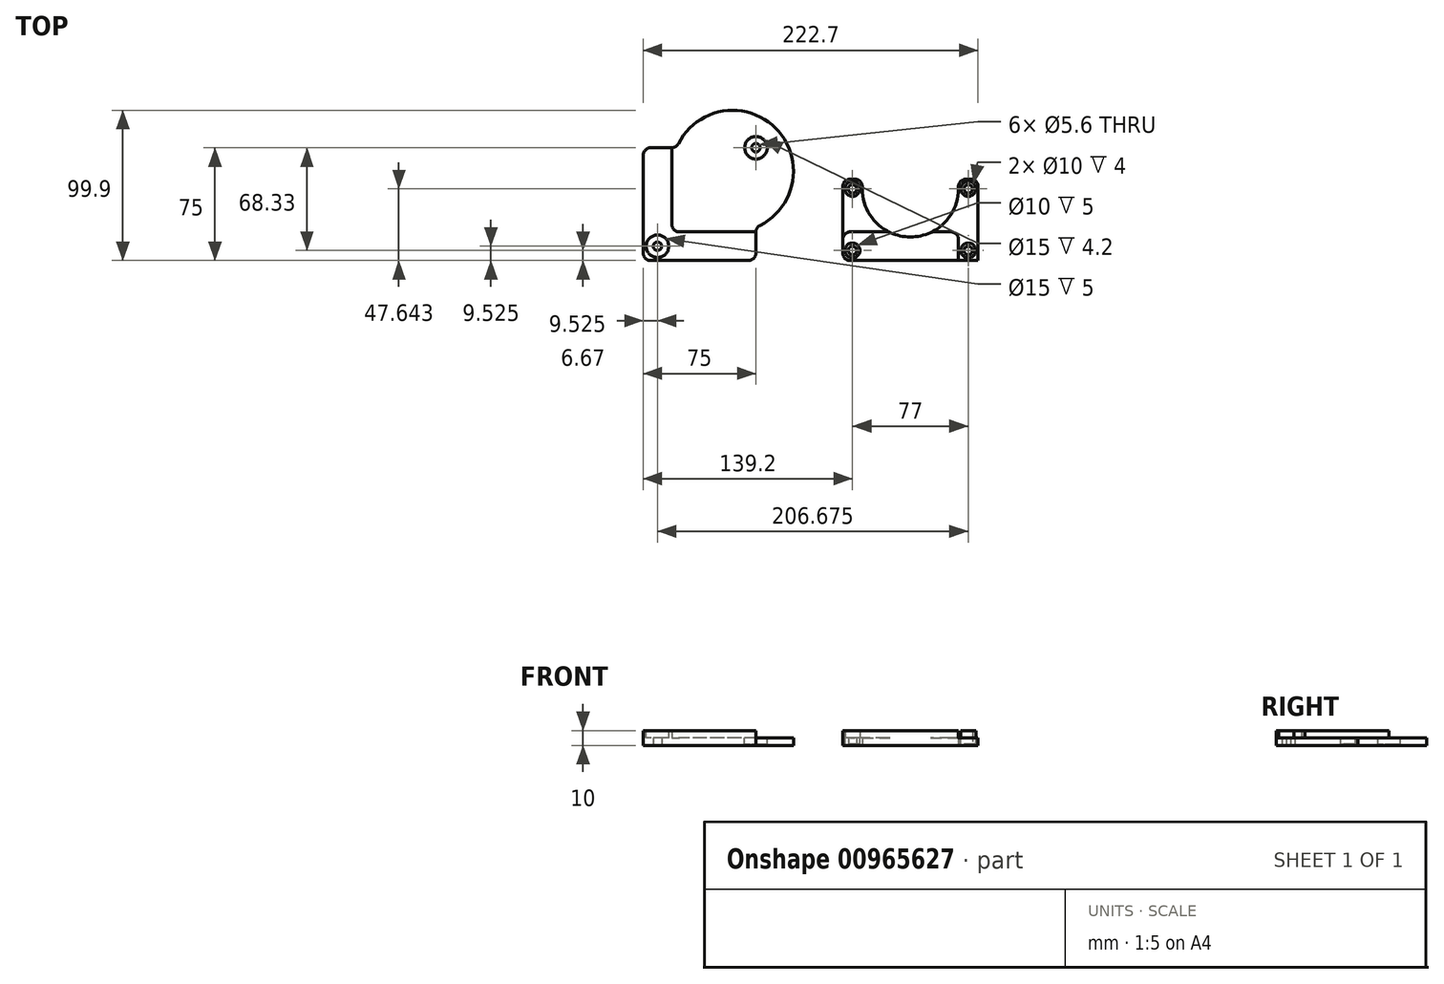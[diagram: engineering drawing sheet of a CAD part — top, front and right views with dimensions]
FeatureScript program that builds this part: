
annotation { "Feature Type Name" : "Feature", "Feature Type Description" : "" }
export const myFeature = defineFeature(function(context is Context, id is Id, definition is map)
    precondition{}
    {
        {
            var Q0;
            Q0=qCreatedBy(makeId("Top.planeOp"),FACE);
            var sketch = newSketch(context, id + "F0", { "sketchPlane" : qUnion([Q0])});
            skLineSegment(sketch, "E0.bottom", {"start": v(37.5, -37.5) * mm, "end": v(-37.5, -37.5) * mm});
            skLineSegment(sketch, "E0.top", {"start": v(37.5, 37.5) * mm, "end": v(-37.5, 37.5) * mm});
            skLineSegment(sketch, "E0.left", {"start": v(37.5, -37.5) * mm, "end": v(37.5, 37.5) * mm});
            skLineSegment(sketch, "E0.right", {"start": v(-37.5, -37.5) * mm, "end": v(-37.5, 37.5) * mm});
            skPoint(sketch, "E0.middle", {"position": v(0, 0) * mm});
            skLineSegment(sketch, "E1", {"start": v(-18.45, 37.5) * mm, "end": v(-18.45, -37.5) * mm});
            skLineSegment(sketch, "E2", {"start": v(-37.5, -18.45) * mm, "end": v(37.5, -18.45) * mm});
            skLineSegment(sketch, "E3", {"start": v(-27.98, -18.45) * mm, "end": v(-27.98, -37.5) * mm, "construction": true});
            skLineSegment(sketch, "E4", {"start": v(-37.5, -27.98) * mm, "end": v(-18.45, -27.98) * mm, "construction": true});
            skPoint(sketch, "E5", {"position": v(-27.98, -27.98) * mm});
            skLineSegment(sketch, "E6", {"start": v(37.5, 37.5) * mm, "end": v(-18.45, -18.45) * mm, "construction": true});
            skCircle(sketch, "E7", {"center": v(21.97, 21.97) * mm, "radius": 40.42 * mm});
            skCircle(sketch, "E8", {"center": v(37.5, 37.5) * mm, "radius": 2.8 * mm});
            skCircle(sketch, "E9", {"center": v(-27.98, -27.98) * mm, "radius": 2.8 * mm});
            skSolve(sketch);
        }
        {
            var Q0;
            {var subQ4=sQuery(id+"F0.wireOp",EDGE,"E0.top");var subQ6=sQuery(id+"F0.wireOp",EDGE,"E0.right");var subQ7=makeQuery(id+"F0.imprint","INTERSECT",VERTEX,{"derivedFrom":[subQ4,subQ6]});Q0=makeQuery(id+"F0.imprint","IMPRINT",FACE,{"disambiguationData":[TD([[makeQuery(id+"F0.imprint","IMPRINT",EDGE,{"disambiguationData":[TD([[subQ7,1.0]])],"derivedFrom":subQ4}),1.0]])]});}
            var Q1;
            Q1=makeQuery(id+"F0.imprint","IMPRINT",FACE,{"disambiguationData":[TD([[makeQuery(id+"F0.imprint","IMPRINT",EDGE,{"derivedFrom":sQuery(id+"F0.wireOp",EDGE,"E9")}),-1.0]])]});
            var Q2;
            {var subQ1=sQuery(id+"F0.wireOp",EDGE,"E0.bottom");var subQ6=sQuery(id+"F0.wireOp",EDGE,"E0.left");var subQ7=makeQuery(id+"F0.imprint","INTERSECT",VERTEX,{"derivedFrom":[subQ1,subQ6]});Q2=makeQuery(id+"F0.imprint","IMPRINT",FACE,{"disambiguationData":[TD([[makeQuery(id+"F0.imprint","IMPRINT",EDGE,{"disambiguationData":[TD([[subQ7,-1.0]])],"derivedFrom":subQ1}),-1.0]])]});}
            var Q3;
            {var subQ0=sQuery(id+"F0.wireOp",EDGE,"E7");var subQ1=sQuery(id+"F0.wireOp",EDGE,"E1");var subQ2=makeQuery(id+"F0.imprint","INTERSECT",VERTEX,{"derivedFrom":[subQ1,subQ0]});Q3=makeQuery(id+"F0.imprint","IMPRINT",FACE,{"disambiguationData":[TD([[makeQuery(id+"F0.imprint","IMPRINT",EDGE,{"disambiguationData":[TD([[subQ2,-1.0]])],"derivedFrom":subQ1}),1.0]])]});}
            var Q4;
            {var subQ0=sQuery(id+"F0.wireOp",EDGE,"E1");var subQ1=sQuery(id+"F0.wireOp",EDGE,"E0.top");var subQ2=makeQuery(id+"F0.imprint","INTERSECT",VERTEX,{"derivedFrom":[subQ1,subQ0]});Q4=makeQuery(id+"F0.imprint","IMPRINT",FACE,{"disambiguationData":[TD([[makeQuery(id+"F0.imprint","IMPRINT",EDGE,{"disambiguationData":[TD([[subQ2,1.0]])],"derivedFrom":subQ1}),1.0]])]});}
            var Q5;
            {var subQ0=sQuery(id+"F0.wireOp",EDGE,"E2");var subQ1=sQuery(id+"F0.wireOp",EDGE,"E0.left");var subQ2=makeQuery(id+"F0.imprint","INTERSECT",VERTEX,{"derivedFrom":[subQ1,subQ0]});Q5=makeQuery(id+"F0.imprint","IMPRINT",FACE,{"disambiguationData":[TD([[makeQuery(id+"F0.imprint","IMPRINT",EDGE,{"disambiguationData":[TD([[subQ2,-1.0]])],"derivedFrom":subQ1}),1.0]])]});}
            var Q6;
            {var subQ0=sQuery(id+"F0.wireOp",EDGE,"E7");var subQ7=sQuery(id+"F0.wireOp",EDGE,"E0.top");var subQ8=makeQuery(id+"F0.imprint","INTERSECT",VERTEX,{"derivedFrom":[subQ7,subQ0]});Q6=makeQuery(id+"F0.imprint","IMPRINT",FACE,{"disambiguationData":[TD([[makeQuery(id+"F0.imprint","IMPRINT",EDGE,{"disambiguationData":[TD([[subQ8,1.0]])],"derivedFrom":subQ7}),1.0]])]});}
            var Q7;
            {var subQ0=sQuery(id+"F0.wireOp",EDGE,"E7");var subQ1=sQuery(id+"F0.wireOp",EDGE,"E0.top");var subQ2=makeQuery(id+"F0.imprint","INTERSECT",VERTEX,{"derivedFrom":[subQ1,subQ0]});Q7=makeQuery(id+"F0.imprint","IMPRINT",FACE,{"disambiguationData":[TD([[makeQuery(id+"F0.imprint","IMPRINT",EDGE,{"disambiguationData":[TD([[subQ2,1.0]])],"derivedFrom":subQ1}),-1.0]])]});}
            extrude(context, id + "F1", {"entities" : qUnion([Q0, Q1, Q2, Q3, Q4, Q5, Q6, Q7]), "depth" : 5 * mm, "offsetDistance" : 25 * mm});
        }
        {
            var Q0;
            {var subQ1=sQuery(id+"F0.wireOp",EDGE,"E0.bottom");var subQ6=sQuery(id+"F0.wireOp",EDGE,"E0.left");var subQ7=makeQuery(id+"F0.imprint","INTERSECT",VERTEX,{"derivedFrom":[subQ1,subQ6]});Q0=makeQuery(id+"F0.imprint","IMPRINT",FACE,{"disambiguationData":[TD([[makeQuery(id+"F0.imprint","IMPRINT",EDGE,{"disambiguationData":[TD([[subQ7,-1.0]])],"derivedFrom":subQ1}),-1.0]])]});}
            var Q1;
            {var subQ4=sQuery(id+"F0.wireOp",EDGE,"E0.top");var subQ6=sQuery(id+"F0.wireOp",EDGE,"E0.right");var subQ7=makeQuery(id+"F0.imprint","INTERSECT",VERTEX,{"derivedFrom":[subQ4,subQ6]});Q1=makeQuery(id+"F0.imprint","IMPRINT",FACE,{"disambiguationData":[TD([[makeQuery(id+"F0.imprint","IMPRINT",EDGE,{"disambiguationData":[TD([[subQ7,1.0]])],"derivedFrom":subQ4}),1.0]])]});}
            var Q2;
            Q2=makeQuery(id+"F0.imprint","IMPRINT",FACE,{"disambiguationData":[TD([[makeQuery(id+"F0.imprint","IMPRINT",EDGE,{"derivedFrom":sQuery(id+"F0.wireOp",EDGE,"E9")}),-1.0]])]});
            extrude(context, id + "F2", {"entities" : qUnion([Q0, Q1, Q2]), "operationType" : NewBodyOperationType.ADD, "depth" : 10 * mm, "offsetDistance" : 25 * mm});
        }
        {
            var Q0;
            Q0=makeQuery(id+"F2.opExtrude","CAP_FACE",FACE,{"disambiguationData":[OSD([sQuery(id+"F0.wireOp",EDGE,"E0.bottom"),sQuery(id+"F0.wireOp",EDGE,"E0.top"),sQuery(id+"F0.wireOp",EDGE,"E0.left"),sQuery(id+"F0.wireOp",EDGE,"E0.right"),sQuery(id+"F0.wireOp",EDGE,"E1"),sQuery(id+"F0.wireOp",EDGE,"E2"),sQuery(id+"F0.wireOp",EDGE,"E9")])],"isStart":false});
            var sketch = newSketch(context, id + "F3", { "sketchPlane" : qUnion([Q0])});
            skCircle(sketch, "E10", {"center": v(-27.98, -27.98) * mm, "radius": 7.5 * mm});
            skSolve(sketch);
        }
        {
            var Q0;
            Q0=makeQuery(id+"F1.opExtrude","CAP_FACE",FACE,{"disambiguationData":[OSD([sQuery(id+"F0.wireOp",EDGE,"E0.bottom"),sQuery(id+"F0.wireOp",EDGE,"E0.top"),sQuery(id+"F0.wireOp",EDGE,"E0.left"),sQuery(id+"F0.wireOp",EDGE,"E0.right"),sQuery(id+"F0.wireOp",EDGE,"E7"),sQuery(id+"F0.wireOp",EDGE,"E8"),sQuery(id+"F0.wireOp",EDGE,"E9")])],"isStart":false});
            var sketch = newSketch(context, id + "F4", { "sketchPlane" : qUnion([Q0])});
            skCircle(sketch, "E11", {"center": v(37.5, 37.5) * mm, "radius": 7.5 * mm});
            skSolve(sketch);
        }
        {
            var Q0;
            Q0=makeQuery(id+"F4.imprint","IMPRINT",FACE,{"disambiguationData":[TD([[makeQuery(id+"F4.imprint","IMPRINT",EDGE,{"derivedFrom":sQuery(id+"F4.wireOp",EDGE,"E11")}),1.0]])]});
            extrude(context, id + "F5", {"entities" : qUnion([Q0]), "operationType" : NewBodyOperationType.REMOVE, "oppositeDirection" : true, "depth" : (5 - .8) * mm, "offsetDistance" : 25 * mm});
        }
        {
            var Q0;
            Q0=makeQuery(id+"F3.imprint","IMPRINT",FACE,{"disambiguationData":[TD([[makeQuery(id+"F3.imprint","IMPRINT",EDGE,{"derivedFrom":sQuery(id+"F3.wireOp",EDGE,"E10")}),1.0]])]});
            extrude(context, id + "F6", {"entities" : qUnion([Q0]), "operationType" : NewBodyOperationType.REMOVE, "oppositeDirection" : true, "depth" : 5 * mm, "offsetDistance" : 25 * mm});
        }
        {
            var Q0;
            Q0=makeQuery(id+"F1.opExtrude","SWEPT_EDGE",EDGE,{"disambiguationData":[OSD([sQuery(id+"F0.wireOp",EDGE,"E0.left"),sQuery(id+"F0.wireOp",EDGE,"E7")])]});
            var Q1;
            Q1=makeQuery(id+"F1.opExtrude","SWEPT_EDGE",EDGE,{"disambiguationData":[OSD([sQuery(id+"F0.wireOp",EDGE,"E0.top"),sQuery(id+"F0.wireOp",EDGE,"E7")])]});
            var Q2;
            Q2=makeQuery(id+"F2.opExtrude","SWEPT_EDGE",EDGE,{"disambiguationData":[OSD([sQuery(id+"F0.wireOp",EDGE,"E1"),sQuery(id+"F0.wireOp",EDGE,"E2")])]});
            var Q3;
            {var subQ0=sQuery(id+"F0.wireOp",EDGE,"E0.right");var subQ1=sQuery(id+"F0.wireOp",EDGE,"E0.bottom");Q3=makeQuery(id+"F2.boolean.opBoolean","MERGE",EDGE,{"derivedFrom":[makeQuery(id+"F1.opExtrude","SWEPT_EDGE",EDGE,{"disambiguationData":[OSD([subQ1,subQ0])]}),makeQuery(id+"F2.opExtrude","SWEPT_EDGE",EDGE,{"disambiguationData":[OSD([subQ1,subQ0])]})]});}
            var Q4;
            {var subQ0=sQuery(id+"F0.wireOp",EDGE,"E0.left");var subQ1=sQuery(id+"F0.wireOp",EDGE,"E0.bottom");Q4=makeQuery(id+"F2.boolean.opBoolean","MERGE",EDGE,{"derivedFrom":[makeQuery(id+"F1.opExtrude","SWEPT_EDGE",EDGE,{"disambiguationData":[OSD([subQ1,subQ0])]}),makeQuery(id+"F2.opExtrude","SWEPT_EDGE",EDGE,{"disambiguationData":[OSD([subQ1,subQ0])]})]});}
            var Q5;
            {var subQ0=sQuery(id+"F0.wireOp",EDGE,"E0.right");var subQ1=sQuery(id+"F0.wireOp",EDGE,"E0.top");Q5=makeQuery(id+"F2.boolean.opBoolean","MERGE",EDGE,{"derivedFrom":[makeQuery(id+"F1.opExtrude","SWEPT_EDGE",EDGE,{"disambiguationData":[OSD([subQ1,subQ0])]}),makeQuery(id+"F2.opExtrude","SWEPT_EDGE",EDGE,{"disambiguationData":[OSD([subQ1,subQ0])]})]});}
            fillet(context, id + "F7", {"entities" : qUnion([Q0, Q1, Q2, Q3, Q4, Q5]), "radius" : 5 * mm, "tangentPropagation" : true, "allowEdgeOverflow" : false});
        }
        {
            var Q0;
            Q0=qCreatedBy(makeId("Top.planeOp"),FACE);
            var sketch = newSketch(context, id + "F8", { "sketchPlane" : qUnion([Q0])});
            skLineSegment(sketch, "E12.bottom", {"start": v(95.2, -37.5) * mm, "end": v(185.2, -37.5) * mm});
            skLineSegment(sketch, "E12.top", {"start": v(95.2, 16.63) * mm, "end": v(108.2, 16.63) * mm});
            skLineSegment(sketch, "E12.left", {"start": v(95.2, -37.5) * mm, "end": v(95.2, 16.63) * mm});
            skLineSegment(sketch, "E12.right", {"start": v(185.2, -37.5) * mm, "end": v(185.2, 16.63) * mm});
            skLineSegment(sketch, "E13", {"start": v(-49.52, -37.5) * mm, "end": v(252.15, -37.5) * mm, "construction": true});
            skLineSegment(sketch, "E14", {"start": v(140.2, 16.63) * mm, "end": v(140.2, -37.5) * mm, "construction": true});
            skArc(sketch, "E15", {"start": v(108.2, 10.14) * mm, "mid": v(140.2, -21.86) * mm, "end": v(172.2, 10.14) * mm});
            skLineSegment(sketch, "E16", {"start": v(172.2, -37.5) * mm, "end": v(172.2, 16.63) * mm});
            skLineSegment(sketch, "E17", {"start": v(108.2, 16.63) * mm, "end": v(108.2, -37.5) * mm});
            skLineSegment(sketch, "E18", {"start": v(95.2, 10.14) * mm, "end": v(185.2, 10.14) * mm, "construction": true});
            skLineSegment(sketch, "E19", {"start": v(101.7, 16.63) * mm, "end": v(101.7, -37.5) * mm, "construction": true});
            skLineSegment(sketch, "E20", {"start": v(178.7, 16.63) * mm, "end": v(178.7, -37.5) * mm, "construction": true});
            skCircle(sketch, "E21", {"center": v(178.7, 10.14) * mm, "radius": 2.8 * mm});
            skCircle(sketch, "E22", {"center": v(101.7, 10.14) * mm, "radius": 2.8 * mm});
            skCircle(sketch, "E23", {"center": v(101.7, 10.14) * mm, "radius": 5 * mm});
            skCircle(sketch, "E24", {"center": v(178.7, 10.14) * mm, "radius": 5 * mm});
            skLineSegment(sketch, "E25.trimOffspring", {"start": v(172.2, 16.63) * mm, "end": v(185.2, 16.63) * mm});
            skLineSegment(sketch, "E26", {"start": v(95.2, -18.45) * mm, "end": v(185.2, -18.45) * mm});
            skCircle(sketch, "E27", {"center": v(101.7, -30.83) * mm, "radius": 2.8 * mm});
            skCircle(sketch, "E28", {"center": v(101.7, -30.83) * mm, "radius": 5 * mm});
            skCircle(sketch, "E29.MirrorC", {"center": v(178.7, -30.83) * mm, "radius": 5 * mm});
            skCircle(sketch, "E30.MirrorC", {"center": v(178.7, -30.83) * mm, "radius": 2.8 * mm});
            skSolve(sketch);
        }
        {
            var Q0;
            {var subQ0=sQuery(id+"F8.wireOp",EDGE,"E15");Q0=makeQuery(id+"F8.imprint","IMPRINT",FACE,{"disambiguationData":[TD([[makeQuery(id+"F8.imprint","IMPRINT",EDGE,{"derivedFrom":subQ0}),-1.0]])]});}
            var Q1;
            {var subQ1=sQuery(id+"F8.wireOp",EDGE,"E12.top");Q1=makeQuery(id+"F8.imprint","IMPRINT",FACE,{"disambiguationData":[TD([[makeQuery(id+"F8.imprint","IMPRINT",EDGE,{"derivedFrom":subQ1}),-1.0]])]});}
            var Q2;
            Q2=makeQuery(id+"F8.imprint","IMPRINT",FACE,{"disambiguationData":[TD([[makeQuery(id+"F8.imprint","IMPRINT",EDGE,{"derivedFrom":sQuery(id+"F8.wireOp",EDGE,"E28")}),-1.0]])]});
            var Q3;
            {var subQ0=sQuery(id+"F8.wireOp",EDGE,"E16");var subQ1=sQuery(id+"F8.wireOp",EDGE,"E12.bottom");var subQ2=makeQuery(id+"F8.imprint","INTERSECT",VERTEX,{"derivedFrom":[subQ1,subQ0]});Q3=makeQuery(id+"F8.imprint","IMPRINT",FACE,{"disambiguationData":[TD([[makeQuery(id+"F8.imprint","IMPRINT",EDGE,{"disambiguationData":[TD([[subQ2,1.0]])],"derivedFrom":subQ1}),1.0]])]});}
            var Q4;
            Q4=makeQuery(id+"F8.imprint","IMPRINT",FACE,{"disambiguationData":[TD([[makeQuery(id+"F8.imprint","IMPRINT",EDGE,{"derivedFrom":sQuery(id+"F8.wireOp",EDGE,"E24")}),-1.0]])]});
            var Q5;
            Q5=makeQuery(id+"F8.imprint","IMPRINT",FACE,{"disambiguationData":[TD([[makeQuery(id+"F8.imprint","IMPRINT",EDGE,{"derivedFrom":sQuery(id+"F8.wireOp",EDGE,"E29.MirrorC")}),1.0]])]});
            var Q6;
            Q6=makeQuery(id+"F8.imprint","IMPRINT",FACE,{"disambiguationData":[TD([[makeQuery(id+"F8.imprint","IMPRINT",EDGE,{"derivedFrom":sQuery(id+"F8.wireOp",EDGE,"E27")}),-1.0]])]});
            var Q7;
            Q7=makeQuery(id+"F8.imprint","IMPRINT",FACE,{"disambiguationData":[TD([[makeQuery(id+"F8.imprint","IMPRINT",EDGE,{"derivedFrom":sQuery(id+"F8.wireOp",EDGE,"E22")}),-1.0]])]});
            var Q8;
            Q8=makeQuery(id+"F8.imprint","IMPRINT",FACE,{"disambiguationData":[TD([[makeQuery(id+"F8.imprint","IMPRINT",EDGE,{"derivedFrom":sQuery(id+"F8.wireOp",EDGE,"E21")}),-1.0]])]});
            var Q9;
            Q9=makeQuery(id+"F8.imprint","IMPRINT",FACE,{"disambiguationData":[TD([[makeQuery(id+"F8.imprint","IMPRINT",EDGE,{"derivedFrom":sQuery(id+"F8.wireOp",EDGE,"E29.MirrorC")}),-1.0]])]});
            extrude(context, id + "F9", {"entities" : qUnion([Q0, Q1, Q2, Q3, Q4, Q5, Q6, Q7, Q8, Q9]), "depth" : 5 * mm, "offsetDistance" : 25 * mm});
        }
        {
            var Q0;
            Q0=makeQuery(id+"F8.imprint","IMPRINT",FACE,{"disambiguationData":[TD([[makeQuery(id+"F8.imprint","IMPRINT",EDGE,{"derivedFrom":sQuery(id+"F8.wireOp",EDGE,"E28")}),-1.0]])]});
            var Q1;
            {var subQ0=sQuery(id+"F8.wireOp",EDGE,"E16");var subQ1=sQuery(id+"F8.wireOp",EDGE,"E12.bottom");var subQ2=makeQuery(id+"F8.imprint","INTERSECT",VERTEX,{"derivedFrom":[subQ1,subQ0]});Q1=makeQuery(id+"F8.imprint","IMPRINT",FACE,{"disambiguationData":[TD([[makeQuery(id+"F8.imprint","IMPRINT",EDGE,{"disambiguationData":[TD([[subQ2,1.0]])],"derivedFrom":subQ1}),1.0]])]});}
            var Q2;
            Q2=makeQuery(id+"F8.imprint","IMPRINT",FACE,{"disambiguationData":[TD([[makeQuery(id+"F8.imprint","IMPRINT",EDGE,{"derivedFrom":sQuery(id+"F8.wireOp",EDGE,"E29.MirrorC")}),1.0]])]});
            extrude(context, id + "F10", {"entities" : qUnion([Q0, Q1, Q2]), "operationType" : NewBodyOperationType.ADD, "depth" : 10 * mm, "offsetDistance" : 25 * mm});
        }
        {
            var Q0;
            {var subQ0=sQuery(id+"F8.wireOp",EDGE,"E25.trimOffspring");var subQ1=sQuery(id+"F8.wireOp",EDGE,"E22");var subQ2=sQuery(id+"F8.wireOp",EDGE,"E21");var subQ3=sQuery(id+"F8.wireOp",EDGE,"E17");var subQ4=sQuery(id+"F8.wireOp",EDGE,"E12.left");var subQ5=sQuery(id+"F8.wireOp",EDGE,"E16");var subQ6=sQuery(id+"F8.wireOp",EDGE,"E12.top");var subQ7=sQuery(id+"F8.wireOp",EDGE,"E12.right");var subQ8=sQuery(id+"F8.wireOp",EDGE,"E15");Q0=makeQuery(id+"F10.boolean.opBoolean","SPLIT",FACE,{"disambiguationData":[TD([makeQuery(id+"F9.opExtrude","SWEPT_FACE",FACE,{"disambiguationData":[OSD([subQ6])]})])],"derivedFrom":makeQuery(id+"F9.opExtrude","CAP_FACE",FACE,{"disambiguationData":[OSD([sQuery(id+"F8.wireOp",EDGE,"E12.bottom"),subQ6,subQ4,subQ7,subQ8,subQ5,subQ3,subQ2,subQ1,subQ0,sQuery(id+"F8.wireOp",EDGE,"E27"),sQuery(id+"F8.wireOp",EDGE,"E30.MirrorC")])],"isStart":false})});}
            var sketch = newSketch(context, id + "F11", { "sketchPlane" : qUnion([Q0])});
            skCircle(sketch, "E31", {"center": v(101.7, 10.14) * mm, "radius": 5 * mm});
            skCircle(sketch, "E32", {"center": v(178.7, 10.14) * mm, "radius": 5 * mm});
            skSolve(sketch);
        }
        {
            var Q0;
            Q0=makeQuery(id+"F11.imprint","IMPRINT",FACE,{"disambiguationData":[TD([[makeQuery(id+"F11.imprint","IMPRINT",EDGE,{"derivedFrom":sQuery(id+"F11.wireOp",EDGE,"E31")}),1.0]])]});
            var Q1;
            Q1=makeQuery(id+"F11.imprint","IMPRINT",FACE,{"disambiguationData":[TD([[makeQuery(id+"F11.imprint","IMPRINT",EDGE,{"derivedFrom":sQuery(id+"F11.wireOp",EDGE,"E32")}),1.0]])]});
            extrude(context, id + "F12", {"entities" : qUnion([Q0, Q1]), "operationType" : NewBodyOperationType.REMOVE, "oppositeDirection" : true, "depth" : 4 * mm, "offsetDistance" : 25 * mm});
        }
        {
            var Q0;
            Q0=makeQuery(id+"F9.opExtrude","SWEPT_EDGE",EDGE,{"disambiguationData":[OSD([sQuery(id+"F8.wireOp",EDGE,"E12.top"),sQuery(id+"F8.wireOp",EDGE,"E12.left")])]});
            var Q1;
            Q1=makeQuery(id+"F9.opExtrude","SWEPT_EDGE",EDGE,{"disambiguationData":[OSD([sQuery(id+"F8.wireOp",EDGE,"E12.top"),sQuery(id+"F8.wireOp",EDGE,"E17")])]});
            var Q2;
            Q2=makeQuery(id+"F9.opExtrude","SWEPT_EDGE",EDGE,{"disambiguationData":[OSD([sQuery(id+"F8.wireOp",EDGE,"E16"),sQuery(id+"F8.wireOp",EDGE,"E25.trimOffspring")])]});
            var Q3;
            Q3=makeQuery(id+"F9.opExtrude","SWEPT_EDGE",EDGE,{"disambiguationData":[OSD([sQuery(id+"F8.wireOp",EDGE,"E12.right"),sQuery(id+"F8.wireOp",EDGE,"E25.trimOffspring")])]});
            var Q4;
            {var subQ0=sQuery(id+"F8.wireOp",EDGE,"E12.left");var subQ1=sQuery(id+"F8.wireOp",EDGE,"E12.bottom");Q4=makeQuery(id+"F10.boolean.opBoolean","MERGE",EDGE,{"derivedFrom":[makeQuery(id+"F9.opExtrude","SWEPT_EDGE",EDGE,{"disambiguationData":[OSD([subQ1,subQ0])]}),makeQuery(id+"F10.opExtrude","SWEPT_EDGE",EDGE,{"disambiguationData":[OSD([subQ1,subQ0])]})]});}
            var Q5;
            {var subQ0=sQuery(id+"F8.wireOp",EDGE,"E12.right");var subQ1=sQuery(id+"F8.wireOp",EDGE,"E12.bottom");Q5=makeQuery(id+"F10.boolean.opBoolean","MERGE",EDGE,{"derivedFrom":[makeQuery(id+"F9.opExtrude","SWEPT_EDGE",EDGE,{"disambiguationData":[OSD([subQ1,subQ0])]}),makeQuery(id+"F10.opExtrude","SWEPT_EDGE",EDGE,{"disambiguationData":[OSD([subQ1,subQ0])]})]});}
            var Q6;
            Q6=makeQuery(id+"F10.opExtrude","SWEPT_EDGE",EDGE,{"disambiguationData":[OSD([sQuery(id+"F8.wireOp",EDGE,"E12.left"),sQuery(id+"F8.wireOp",EDGE,"E26")])]});
            var Q7;
            Q7=makeQuery(id+"F10.opExtrude","SWEPT_EDGE",EDGE,{"disambiguationData":[OSD([sQuery(id+"F8.wireOp",EDGE,"E12.right"),sQuery(id+"F8.wireOp",EDGE,"E26")])]});
            fillet(context, id + "F13", {"entities" : qUnion([Q0, Q1, Q2, Q3, Q4, Q5, Q6, Q7]), "radius" : 5 * mm, "tangentPropagation" : true, "allowEdgeOverflow" : false});
        }
    });
